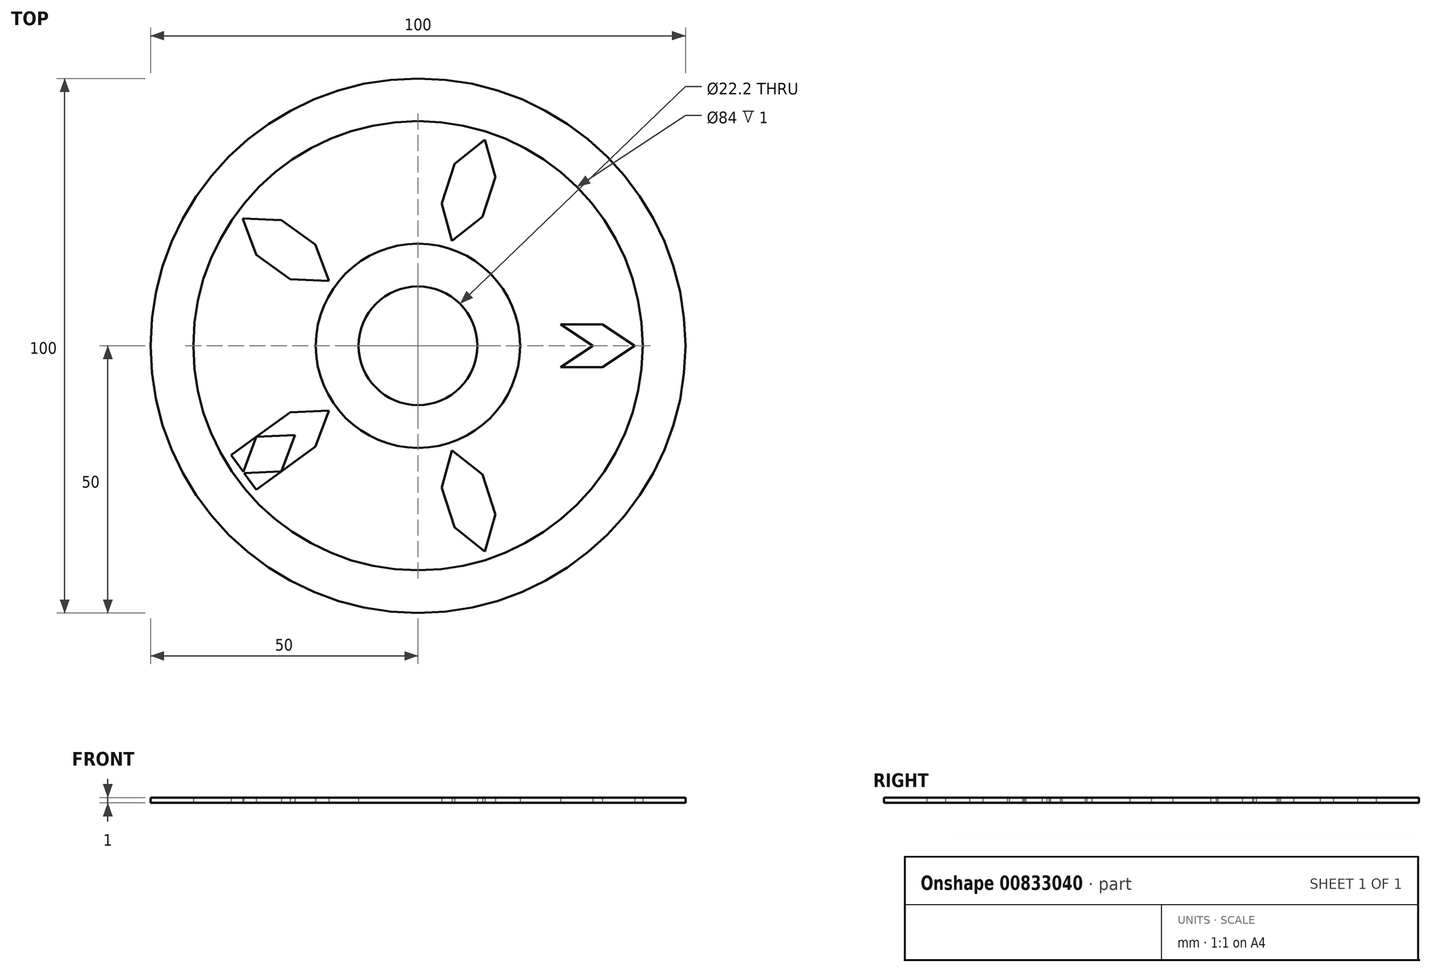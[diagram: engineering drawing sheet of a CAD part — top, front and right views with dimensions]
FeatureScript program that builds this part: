
annotation { "Feature Type Name" : "Feature", "Feature Type Description" : "" }
export const myFeature = defineFeature(function(context is Context, id is Id, definition is map)
    precondition{}
    {
        {
            var Q0;
            Q0=qCreatedBy(makeId("Top.planeOp"),FACE);
            var sketch = newSketch(context, id + "F0", { "sketchPlane" : qUnion([Q0])});
            skCircle(sketch, "E0", {"center": v(0, 0) * mm, "radius": 19.1 * mm, "construction": true});
            skCircle(sketch, "E1", {"center": v(0, 0) * mm, "radius": 42 * mm, "construction": true});
            skLineSegment(sketch, "E2", {"start": v(0, 0) * mm, "end": v(-33.98, -24.69) * mm, "construction": true});
            skLineSegment(sketch, "E3", {"start": v(-17.46, -7.74) * mm, "end": v(-36.33, -21.45) * mm, "construction": true});
            skLineSegment(sketch, "E4", {"start": v(-36.33, -21.45) * mm, "end": v(-31.63, -27.92) * mm, "construction": true});
            skLineSegment(sketch, "E5", {"start": v(-31.63, -27.92) * mm, "end": v(-12.76, -14.21) * mm, "construction": true});
            skCircle(sketch, "E6", {"center": v(0, 0) * mm, "radius": 50 * mm, "construction": true});
            skCircle(sketch, "E7", {"center": v(0, 0) * mm, "radius": 11.1 * mm, "construction": true});
            skLineSegment(sketch, "E8", {"start": v(-17.46, -7.74) * mm, "end": v(-12.76, -14.21) * mm, "construction": true});
            skSolve(sketch);
        }
        {
            var Q0;
            Q0=qCreatedBy(makeId("Top.planeOp"),FACE);
            var sketch = newSketch(context, id + "F1", { "sketchPlane" : qUnion([Q0])});
            skLineSegment(sketch, "E9", {"start": v(-31.63, -27.92) * mm, "end": v(-12.76, -14.21) * mm});
            skLineSegment(sketch, "E10.MirrorCS", {"start": v(-36.33, -21.45) * mm, "end": v(-17.46, -7.74) * mm});
            skLineSegment(sketch, "E11", {"start": v(-36.33, -21.45) * mm, "end": v(-31.63, -27.92) * mm});
            skLineSegment(sketch, "E12", {"start": v(-17.46, -7.74) * mm, "end": v(-12.76, -14.21) * mm});
            skSolve(sketch);
        }
        {
            var Q0;
            Q0=qCreatedBy(makeId("Top.planeOp"),FACE);
            var sketch = newSketch(context, id + "F2", { "sketchPlane" : qUnion([Q0])});
            skLineSegment(sketch, "E13", {"start": v(-16.66, -12.1) * mm, "end": v(-23.9, -12.42) * mm, "construction": true});
            skLineSegment(sketch, "E14", {"start": v(-16.66, -12.1) * mm, "end": v(-19.2, -18.9) * mm, "construction": true});
            skLineSegment(sketch, "E15", {"start": v(-32.77, -23.8) * mm, "end": v(-30.23, -17.02) * mm, "construction": true});
            skLineSegment(sketch, "E16", {"start": v(-25.52, -23.49) * mm, "end": v(-32.77, -23.8) * mm, "construction": true});
            skSolve(sketch);
        }
        {
            var Q0;
            Q0=qCreatedBy(makeId("Top.planeOp"),FACE);
            var sketch = newSketch(context, id + "F3", { "sketchPlane" : qUnion([Q0])});
            skLineSegment(sketch, "E17.bottom", {"start": v(-275, 50) * mm, "end": v(-60, 50) * mm, "construction": true});
            skLineSegment(sketch, "E17.top", {"start": v(-275, -50) * mm, "end": v(-60, -50) * mm, "construction": true});
            skLineSegment(sketch, "E17.left", {"start": v(-275, 50) * mm, "end": v(-275, -50) * mm, "construction": true});
            skLineSegment(sketch, "E17.right", {"start": v(-60, 50) * mm, "end": v(-60, -50) * mm, "construction": true});
            skLineSegment(sketch, "E18.bottom", {"start": v(-275, -25.39) * mm, "end": v(-40.45, -25.39) * mm, "construction": true});
            skLineSegment(sketch, "E18.top", {"start": v(-275, -33.39) * mm, "end": v(-40.45, -33.39) * mm, "construction": true});
            skLineSegment(sketch, "E18.left", {"start": v(-275, -25.39) * mm, "end": v(-275, -33.39) * mm, "construction": true});
            skLineSegment(sketch, "E18.right", {"start": v(-40.45, -25.39) * mm, "end": v(-40.45, -33.39) * mm, "construction": true});
            skLineSegment(sketch, "E19", {"start": v(-275, -29.39) * mm, "end": v(-40.45, -29.39) * mm, "construction": true});
            skLineSegment(sketch, "E20.bottom", {"start": v(-170, -57.5) * mm, "end": v(50, -57.5) * mm, "construction": true});
            skLineSegment(sketch, "E20.top", {"start": v(-170, -73.5) * mm, "end": v(50, -73.5) * mm, "construction": true});
            skLineSegment(sketch, "E20.left", {"start": v(-170, -57.5) * mm, "end": v(-170, -73.5) * mm, "construction": true});
            skLineSegment(sketch, "E20.right", {"start": v(50, -57.5) * mm, "end": v(50, -73.5) * mm, "construction": true});
            skLineSegment(sketch, "E21", {"start": v(-60, 0) * mm, "end": v(-50, 0) * mm, "construction": true});
            skLineSegment(sketch, "E22", {"start": v(0, -57.5) * mm, "end": v(0, -50) * mm});
            skSolve(sketch);
        }
        {
            var Q0;
            Q0=qSketchRegion(id+"F1",true);
            extrude(context, id + "F4", {"entities" : qUnion([Q0]), "depth" : 1 * mm, "offsetDistance" : 25 * mm});
        }
        {
            var Q0;
            Q0=qCreatedBy(makeId("Top.planeOp"),FACE);
            var sketch = newSketch(context, id + "F5", { "sketchPlane" : qUnion([Q0])});
            skLineSegment(sketch, "E23.0", {"start": v(-32.77, -23.8) * mm, "end": v(-30.23, -17.02) * mm});
            skLineSegment(sketch, "E24.0", {"start": v(-25.52, -23.49) * mm, "end": v(-32.77, -23.8) * mm});
            skLineSegment(sketch, "E25.0", {"start": v(-36.33, -21.45) * mm, "end": v(-31.63, -27.92) * mm});
            skLineSegment(sketch, "E26.0", {"start": v(-31.63, -27.92) * mm, "end": v(-25.52, -23.49) * mm});
            skLineSegment(sketch, "E27.0", {"start": v(-30.23, -17.02) * mm, "end": v(-36.33, -21.45) * mm});
            skPoint(sketch, "E28.orphan", {"position": v(-12.76, -14.21) * mm});
            skPoint(sketch, "E29.orphan", {"position": v(-17.46, -7.74) * mm});
            skLineSegment(sketch, "E30", {"start": v(-23.9, -12.42) * mm, "end": v(-17.46, -7.74) * mm});
            skLineSegment(sketch, "E31", {"start": v(-17.46, -7.74) * mm, "end": v(-12.76, -14.21) * mm});
            skLineSegment(sketch, "E32", {"start": v(-12.76, -14.21) * mm, "end": v(-19.2, -18.9) * mm});
            skLineSegment(sketch, "E33", {"start": v(-19.2, -18.9) * mm, "end": v(-16.66, -12.1) * mm});
            skLineSegment(sketch, "E34", {"start": v(-16.66, -12.1) * mm, "end": v(-23.9, -12.42) * mm});
            skSolve(sketch);
        }
        {
            var Q0;
            Q0=qSketchRegion(id+"F5",true);
            var Q1;
            Q1=makeQuery(id+"F4.opExtrude","CAP_FACE",FACE,{"disambiguationData":[OSD([sQuery(id+"F1.wireOp",EDGE,"E9"),sQuery(id+"F1.wireOp",EDGE,"E10.MirrorCS"),sQuery(id+"F1.wireOp",EDGE,"E11"),sQuery(id+"F1.wireOp",EDGE,"E12")])],"isStart":false});
            extrude(context, id + "F6", {"entities" : qUnion([Q0]), "operationType" : NewBodyOperationType.REMOVE, "endBound" : BoundingType.UP_TO_SURFACE, "depth" : 25 * mm, "endBoundEntityFace" : qUnion([Q1]), "offsetDistance" : 25 * mm});
        }
        {
            var Q0;
            Q0=qCreatedBy(makeId("Front.planeOp"),FACE);
            var sketch = newSketch(context, id + "F7", { "sketchPlane" : qUnion([Q0])});
            skLineSegment(sketch, "E35", {"start": v(0, 0) * mm, "end": v(0, 34.6) * mm, "construction": true});
            skSolve(sketch);
        }
        {
            var Q0;
            Q0=makeQuery(id+"F4.opExtrude","SWEPT_BODY",BODY,{"disambiguationData":[OSD([sQuery(id+"F1.wireOp",EDGE,"E9"),sQuery(id+"F1.wireOp",EDGE,"E10.MirrorCS"),sQuery(id+"F1.wireOp",EDGE,"SYlQ86mh-PDJs-R6Ng-qes8-MsBRZGDtcNO6"),sQuery(id+"F1.wireOp",EDGE,"E11")])]});
            var Q1;
            Q1=sQuery(id+"F7.wireOp",EDGE,"E35");
            circularPattern(context, id + "F8", {"operationType" : NewBodyOperationType.ADD, "entities" : qUnion([Q0]), "axis" : qUnion([Q1]), "angle" : 360 * degree, "instanceCount" : 5, "equalSpace" : true});
        }
        {
            var Q0;
            Q0=qCreatedBy(makeId("Top.planeOp"),FACE);
            var sketch = newSketch(context, id + "F9", { "sketchPlane" : qUnion([Q0])});
            skCircle(sketch, "E36", {"center": v(0, 0) * mm, "radius": 19.1 * mm});
            skSolve(sketch);
        }
        {
            var Q0;
            Q0=qCreatedBy(makeId("Top.planeOp"),FACE);
            var sketch = newSketch(context, id + "F10", { "sketchPlane" : qUnion([Q0])});
            skCircle(sketch, "E37", {"center": v(0, 0) * mm, "radius": 11.1 * mm});
            skSolve(sketch);
        }
        {
            var Q0;
            Q0=qSketchRegion(id+"F9",true);
            var Q1;
            Q1=makeQuery(id+"F9.imprint","IMPRINT",FACE,{"disambiguationData":[TD([[makeQuery(id+"F9.imprint","IMPRINT",EDGE,{"derivedFrom":sQuery(id+"F9.wireOp",EDGE,"E36")}),1.0]])]});
            extrude(context, id + "F11", {"entities" : qUnion([Q0, Q1]), "operationType" : NewBodyOperationType.ADD, "depth" : 1 * mm, "offsetDistance" : 25 * mm});
        }
        {
            var Q0;
            Q0=qSketchRegion(id+"F10",true);
            extrude(context, id + "F12", {"entities" : qUnion([Q0]), "operationType" : NewBodyOperationType.REMOVE, "endBound" : BoundingType.THROUGH_ALL, "depth" : 25 * mm, "offsetDistance" : 25 * mm});
        }
        {
            var Q0;
            Q0=qCreatedBy(makeId("Top.planeOp"),FACE);
            var sketch = newSketch(context, id + "F13", { "sketchPlane" : qUnion([Q0])});
            skCircle(sketch, "E38", {"center": v(0, 0) * mm, "radius": 42 * mm});
            skCircle(sketch, "E39", {"center": v(0, 0) * mm, "radius": 50 * mm});
            skSolve(sketch);
        }
        {
            var Q0;
            Q0=qSketchRegion(id+"F13",true);
            var Q1;
            {var subQ0=makeQuery(id+"F4.opExtrude","CAP_FACE",FACE,{"disambiguationData":[OSD([sQuery(id+"F1.wireOp",EDGE,"E9"),sQuery(id+"F1.wireOp",EDGE,"E10.MirrorCS"),sQuery(id+"F1.wireOp",EDGE,"SYlQ86mh-PDJs-R6Ng-qes8-MsBRZGDtcNO6"),sQuery(id+"F1.wireOp",EDGE,"E11")])],"isStart":false});Q1=makeQuery(id+"F11.boolean.opBoolean","MERGE",FACE,{"derivedFrom":[makeQuery(id+"F8.boolean.opBoolean","MERGE",FACE,{"derivedFrom":[subQ0,makeQuery(id+"F8.opPattern","COPY",FACE,{"derivedFrom":subQ0,"instanceName":"1"}),makeQuery(id+"F8.opPattern","COPY",FACE,{"derivedFrom":subQ0,"instanceName":"2"}),makeQuery(id+"F8.opPattern","COPY",FACE,{"derivedFrom":subQ0,"instanceName":"3"}),makeQuery(id+"F8.opPattern","COPY",FACE,{"derivedFrom":subQ0,"instanceName":"4"}),makeQuery(id+"F8.opPattern","COPY",FACE,{"derivedFrom":subQ0,"instanceName":"5"}),makeQuery(id+"F8.opPattern","COPY",FACE,{"derivedFrom":subQ0,"instanceName":"6"}),makeQuery(id+"F8.opPattern","COPY",FACE,{"derivedFrom":subQ0,"instanceName":"7"}),makeQuery(id+"F8.opPattern","COPY",FACE,{"derivedFrom":subQ0,"instanceName":"8"}),makeQuery(id+"F8.opPattern","COPY",FACE,{"derivedFrom":subQ0,"instanceName":"9"}),makeQuery(id+"F8.opPattern","COPY",FACE,{"derivedFrom":subQ0,"instanceName":"10"}),makeQuery(id+"F8.opPattern","COPY",FACE,{"derivedFrom":subQ0,"instanceName":"11"})]}),makeQuery(id+"F11.opExtrude","CAP_FACE",FACE,{"disambiguationData":[OSD([sQuery(id+"F9.wireOp",EDGE,"E36")])],"isStart":false})]});}
            extrude(context, id + "F14", {"entities" : qUnion([Q0]), "operationType" : NewBodyOperationType.ADD, "endBound" : BoundingType.UP_TO_SURFACE, "depth" : 25 * mm, "endBoundEntityFace" : qUnion([Q1]), "offsetDistance" : 25 * mm});
        }
        {
            var Q0;
            Q0=qCreatedBy(makeId("Top.planeOp"),FACE);
            var sketch = newSketch(context, id + "F15", { "sketchPlane" : qUnion([Q0])});
            skCircle(sketch, "E40", {"center": v(0, 0) * mm, "radius": 42 * mm});
            skCircle(sketch, "E41", {"center": v(0, 0) * mm, "radius": 40.5 * mm});
            skSolve(sketch);
        }
        {
            var Q0;
            Q0=makeQuery(id+"F15.imprint","IMPRINT",FACE,{"disambiguationData":[TD([[makeQuery(id+"F15.imprint","IMPRINT",EDGE,{"derivedFrom":sQuery(id+"F15.wireOp",EDGE,"E40")}),1.0]])]});
            extrude(context, id + "F16", {"entities" : qUnion([Q0]), "operationType" : NewBodyOperationType.REMOVE, "endBound" : BoundingType.THROUGH_ALL, "depth" : 25 * mm, "offsetDistance" : 25 * mm});
        }
        {
            var Q0;
            Q0=qCreatedBy(makeId("Top.planeOp"),FACE);
            var sketch = newSketch(context, id + "F17", { "sketchPlane" : qUnion([Q0])});
            skCircle(sketch, "E42", {"center": v(0, 0) * mm, "radius": 19.1 * mm});
            skCircle(sketch, "E43", {"center": v(0, 0) * mm, "radius": 20.6 * mm});
            skSolve(sketch);
        }
        {
            var Q0;
            Q0=qCreatedBy(makeId("Top.planeOp"),FACE);
            var sketch = newSketch(context, id + "F18", { "sketchPlane" : qUnion([Q0])});
            skCircle(sketch, "E44", {"center": v(0, 0) * mm, "radius": 40.5 * mm, "construction": true});
            skLineSegment(sketch, "E45", {"start": v(-30.23, -17.02) * mm, "end": v(-34.96, -20.45) * mm});
            skLineSegment(sketch, "E46", {"start": v(-34.96, -20.45) * mm, "end": v(-30.25, -26.92) * mm});
            skLineSegment(sketch, "E47", {"start": v(-30.25, -26.92) * mm, "end": v(-25.52, -23.49) * mm});
            skLineSegment(sketch, "E48", {"start": v(-25.52, -23.49) * mm, "end": v(-30.23, -17.02) * mm});
            skSolve(sketch);
        }
        {
            var Q0;
            Q0=makeQuery(id+"F18.imprint","IMPRINT",FACE,{"disambiguationData":[TD([[makeQuery(id+"F18.imprint","IMPRINT",EDGE,{"derivedFrom":sQuery(id+"F18.wireOp",EDGE,"E45")}),1.0]])]});
            extrude(context, id + "F19", {"entities" : qUnion([Q0]), "operationType" : NewBodyOperationType.ADD, "depth" : 1 * mm, "offsetDistance" : 25 * mm});
        }
        {
            var Q0;
            Q0=qCreatedBy(makeId("Top.planeOp"),FACE);
            var sketch = newSketch(context, id + "F20", { "sketchPlane" : qUnion([Q0])});
            skLineSegment(sketch, "E49.0", {"start": v(-22.99, -16.7) * mm, "end": v(-30.23, -17.02) * mm});
            skLineSegment(sketch, "E49.3", {"start": v(-32.77, -23.8) * mm, "end": v(-25.52, -23.49) * mm});
            skLineSegment(sketch, "E50", {"start": v(-30.23, -17.02) * mm, "end": v(-32.77, -23.8) * mm});
            skLineSegment(sketch, "E51", {"start": v(-22.99, -16.7) * mm, "end": v(-25.52, -23.49) * mm});
            skLineSegment(sketch, "E52", {"start": v(20.6, 0) * mm, "end": v(26.64, 4) * mm});
            skLineSegment(sketch, "E53", {"start": v(26.64, 4) * mm, "end": v(32.68, 0) * mm});
            skLineSegment(sketch, "E54", {"start": v(32.68, 0) * mm, "end": v(26.64, -4) * mm});
            skLineSegment(sketch, "E55", {"start": v(26.64, -4) * mm, "end": v(20.6, 0) * mm});
            skSolve(sketch);
        }
        {
            var Q0;
            Q0 = qSketchRegion(id + "F20", true);
            extrude(context, id + "F21", {"entities" : qUnion([Q0]), "operationType" : NewBodyOperationType.REMOVE, "endBound" : BoundingType.THROUGH_ALL, "depth" : 25 * mm, "offsetDistance" : 25 * mm});
        }
        {
            var Q0;
            Q0=qSketchRegion(id+"F17",true);
            extrude(context, id + "F22", {"entities" : qUnion([Q0]), "operationType" : NewBodyOperationType.REMOVE, "endBound" : BoundingType.THROUGH_ALL, "depth" : 25 * mm, "offsetDistance" : 25 * mm});
        }
        {
            var Q0;
            Q0=makeQuery(id+"F20.imprint","IMPRINT",FACE,{"disambiguationData":[TD([[makeQuery(id+"F20.imprint","IMPRINT",EDGE,{"derivedFrom":sQuery(id+"F20.wireOp",EDGE,"E49.0")}),1.0]])]});
            extrude(context, id + "F23", {"entities" : qUnion([Q0]), "operationType" : NewBodyOperationType.REMOVE, "endBound" : BoundingType.THROUGH_ALL, "depth" : 25 * mm, "offsetDistance" : 25 * mm});
        }
    });
